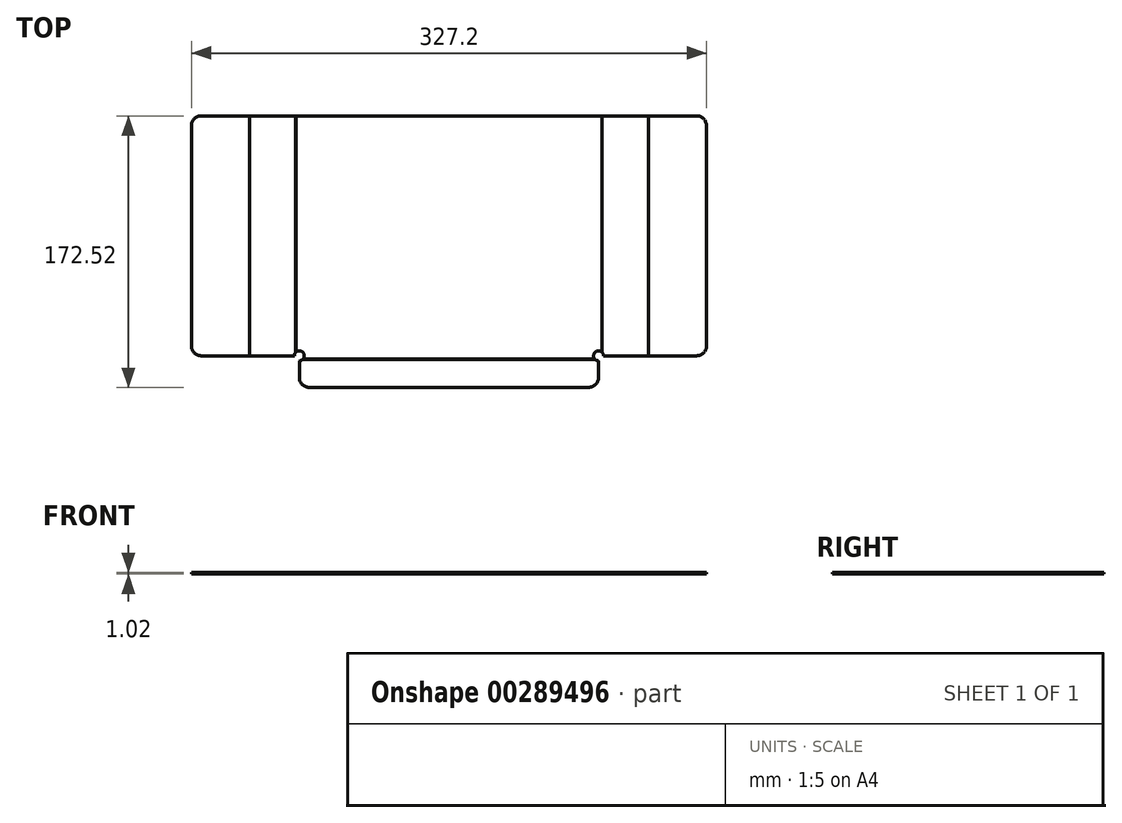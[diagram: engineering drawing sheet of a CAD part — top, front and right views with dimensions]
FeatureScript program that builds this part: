
annotation { "Feature Type Name" : "Feature", "Feature Type Description" : "" }
export const myFeature = defineFeature(function(context is Context, id is Id, definition is map)
    precondition{}
    {
        {
            var Q0;
            Q0=qCreatedBy(makeId("Top.planeOp"),FACE);
            var sketch = newSketch(context, id + "F0", { "sketchPlane" : qUnion([Q0])});
            skLineSegment(sketch, "E0", {"start": v(-95.02, 0) * mm, "end": v(95.02, 0) * mm});
            skPoint(sketch, "E1", {"position": v(0, 0) * mm});
            skLineSegment(sketch, "E2", {"start": v(95.02, 0) * mm, "end": v(99.5, 0) * mm});
            skLineSegment(sketch, "E3", {"start": v(99.5, 0) * mm, "end": v(124.43, 0) * mm});
            skLineSegment(sketch, "E4", {"start": v(124.43, 0) * mm, "end": v(128.9, 0) * mm});
            skLineSegment(sketch, "E5", {"start": v(128.9, 0) * mm, "end": v(157.25, 0) * mm});
            skLineSegment(sketch, "E6", {"start": v(163.6, 6.35) * mm, "end": v(163.6, 146.05) * mm});
            skLineSegment(sketch, "E7", {"start": v(157.25, 152.4) * mm, "end": v(128.9, 152.4) * mm});
            skLineSegment(sketch, "E8", {"start": v(128.9, 152.4) * mm, "end": v(124.43, 152.4) * mm});
            skLineSegment(sketch, "E9", {"start": v(124.43, 152.4) * mm, "end": v(99.5, 152.4) * mm});
            skLineSegment(sketch, "E10", {"start": v(99.5, 152.4) * mm, "end": v(95.02, 152.4) * mm});
            skLineSegment(sketch, "E11", {"start": v(95.02, 152.4) * mm, "end": v(-95.02, 152.4) * mm});
            skLineSegment(sketch, "E12", {"start": v(0, 0) * mm, "end": v(0, 152.4) * mm, "construction": true});
            skLineSegment(sketch, "E13.MirrorCS", {"start": v(-99.5, 152.4) * mm, "end": v(-95.02, 152.4) * mm});
            skLineSegment(sketch, "E14.MirrorCS", {"start": v(-124.43, 152.4) * mm, "end": v(-99.5, 152.4) * mm});
            skLineSegment(sketch, "E15.MirrorCS", {"start": v(-128.9, 152.4) * mm, "end": v(-124.43, 152.4) * mm});
            skLineSegment(sketch, "E16.MirrorCS", {"start": v(-157.25, 152.4) * mm, "end": v(-128.9, 152.4) * mm});
            skLineSegment(sketch, "E17.MirrorCS", {"start": v(-163.6, 6.35) * mm, "end": v(-163.6, 146.05) * mm});
            skLineSegment(sketch, "E18.MirrorCS", {"start": v(-128.9, 0) * mm, "end": v(-157.25, 0) * mm});
            skLineSegment(sketch, "E19.MirrorCS", {"start": v(-124.43, 0) * mm, "end": v(-128.9, 0) * mm});
            skLineSegment(sketch, "E20.MirrorCS", {"start": v(-99.5, 0) * mm, "end": v(-124.43, 0) * mm});
            skLineSegment(sketch, "E21.MirrorCS", {"start": v(-95.02, 0) * mm, "end": v(-99.5, 0) * mm});
            skPoint(sketch, "E22", {"position": v(126.67, 0) * mm});
            skPoint(sketch, "E23", {"position": v(97.26, 0) * mm});
            skPoint(sketch, "E24", {"position": v(-97.26, 0) * mm});
            skPoint(sketch, "E25", {"position": v(-126.67, 0) * mm});
            skLineSegment(sketch, "E26", {"start": v(-126.67, 0) * mm, "end": v(-126.67, 152.4) * mm, "construction": true});
            skLineSegment(sketch, "E27", {"start": v(-97.26, 0) * mm, "end": v(-97.26, 152.4) * mm, "construction": true});
            skLineSegment(sketch, "E28", {"start": v(97.26, 0) * mm, "end": v(97.26, 152.4) * mm, "construction": true});
            skLineSegment(sketch, "E29", {"start": v(126.67, 0) * mm, "end": v(126.67, 152.4) * mm, "construction": true});
            skLineSegment(sketch, "E30.bottom", {"start": v(-97.32, 152.4) * mm, "end": v(-97.2, 152.4) * mm});
            skLineSegment(sketch, "E30.top", {"start": v(-97.32, 0) * mm, "end": v(-97.2, 0) * mm});
            skLineSegment(sketch, "E30.left", {"start": v(-97.32, 152.4) * mm, "end": v(-97.32, 0) * mm});
            skLineSegment(sketch, "E30.right", {"start": v(-97.2, 152.4) * mm, "end": v(-97.2, 0) * mm});
            skPoint(sketch, "E31", {"position": v(-97.26, 152.4) * mm});
            skLineSegment(sketch, "E32.bottom", {"start": v(-126.73, 152.4) * mm, "end": v(-126.6, 152.4) * mm});
            skLineSegment(sketch, "E32.top", {"start": v(-126.73, 0) * mm, "end": v(-126.6, 0) * mm});
            skLineSegment(sketch, "E32.left", {"start": v(-126.73, 152.4) * mm, "end": v(-126.73, 0) * mm});
            skLineSegment(sketch, "E32.right", {"start": v(-126.6, 152.4) * mm, "end": v(-126.6, 0) * mm});
            skLineSegment(sketch, "E33.MirrorCS", {"start": v(97.2, 152.4) * mm, "end": v(97.2, 0) * mm});
            skLineSegment(sketch, "E34.MirrorCS", {"start": v(97.32, 152.4) * mm, "end": v(97.32, 0) * mm});
            skLineSegment(sketch, "E35.MirrorCS", {"start": v(126.6, 152.4) * mm, "end": v(126.6, 0) * mm});
            skLineSegment(sketch, "E36.MirrorCS", {"start": v(126.73, 152.4) * mm, "end": v(126.73, 0) * mm});
            skPoint(sketch, "E37.visualSharp", {"position": v(163.6, 152.4) * mm});
            skArc(sketch, "E37.filletArc", {"start": v(163.6, 146.05) * mm, "mid": v(161.74, 150.54) * mm, "end": v(157.25, 152.4) * mm});
            skPoint(sketch, "E38.visualSharp", {"position": v(163.6, 0) * mm});
            skArc(sketch, "E38.filletArc", {"start": v(157.25, 0) * mm, "mid": v(161.74, 1.86) * mm, "end": v(163.6, 6.35) * mm});
            skPoint(sketch, "E39.visualSharp", {"position": v(-163.6, 0) * mm});
            skArc(sketch, "E39.filletArc", {"start": v(-163.6, 6.35) * mm, "mid": v(-161.74, 1.86) * mm, "end": v(-157.25, 0) * mm});
            skPoint(sketch, "E40.visualSharp", {"position": v(-163.6, 152.4) * mm});
            skArc(sketch, "E40.filletArc", {"start": v(-157.25, 152.4) * mm, "mid": v(-161.74, 150.54) * mm, "end": v(-163.6, 146.05) * mm});
            skLineSegment(sketch, "E41.top", {"start": v(-95.02, -4.47) * mm, "end": v(95.02, -4.47) * mm});
            skLineSegment(sketch, "E41.left", {"start": v(-95.02, 0) * mm, "end": v(-95.02, -4.47) * mm});
            skLineSegment(sketch, "E41.right", {"start": v(95.02, 0) * mm, "end": v(95.02, -4.47) * mm});
            skLineSegment(sketch, "E42.bottom", {"start": v(95.02, -4.47) * mm, "end": v(-95.02, -4.47) * mm});
            skLineSegment(sketch, "E42.top", {"start": v(88.67, -20.12) * mm, "end": v(-88.67, -20.12) * mm});
            skLineSegment(sketch, "E42.left", {"start": v(95.02, -4.47) * mm, "end": v(95.02, -13.77) * mm});
            skLineSegment(sketch, "E42.right", {"start": v(-95.02, -4.47) * mm, "end": v(-95.02, -13.77) * mm});
            skPoint(sketch, "E43", {"position": v(-95.02, -2.24) * mm});
            skLineSegment(sketch, "E44.bottom", {"start": v(-95.02, -2.17) * mm, "end": v(95.02, -2.17) * mm});
            skLineSegment(sketch, "E44.top", {"start": v(-95.02, -2.3) * mm, "end": v(95.02, -2.3) * mm});
            skLineSegment(sketch, "E44.left", {"start": v(-95.02, -2.17) * mm, "end": v(-95.02, -2.3) * mm});
            skLineSegment(sketch, "E44.right", {"start": v(95.02, -2.17) * mm, "end": v(95.02, -2.3) * mm});
            skLineSegment(sketch, "E45", {"start": v(-95.02, -2.24) * mm, "end": v(95.02, -2.24) * mm, "construction": true});
            skPoint(sketch, "E46.visualSharp", {"position": v(-95.02, -20.12) * mm});
            skArc(sketch, "E46.filletArc", {"start": v(-95.02, -13.77) * mm, "mid": v(-93.16, -18.26) * mm, "end": v(-88.67, -20.12) * mm});
            skPoint(sketch, "E47.visualSharp", {"position": v(95.02, -20.12) * mm});
            skArc(sketch, "E47.filletArc", {"start": v(88.67, -20.12) * mm, "mid": v(93.16, -18.26) * mm, "end": v(95.02, -13.77) * mm});
            skSolve(sketch);
        }
        {
            var Q0;
            Q0=qSketchRegion(id+"F0",true);
            extrude(context, id + "F1", {"entities" : qUnion([Q0]), "depth" : 1.02 * mm});
        }
        {
            var Q0;
            Q0=makeQuery(id+"F1.opExtrude","CAP_FACE",FACE,{"disambiguationData":[OSD([sQuery(id+"F0.wireOp",EDGE,"E2"),sQuery(id+"F0.wireOp",EDGE,"E3"),sQuery(id+"F0.wireOp",EDGE,"E4"),sQuery(id+"F0.wireOp",EDGE,"E5"),sQuery(id+"F0.wireOp",EDGE,"E6"),sQuery(id+"F0.wireOp",EDGE,"E7"),sQuery(id+"F0.wireOp",EDGE,"E8"),sQuery(id+"F0.wireOp",EDGE,"E9"),sQuery(id+"F0.wireOp",EDGE,"E10"),sQuery(id+"F0.wireOp",EDGE,"E11"),sQuery(id+"F0.wireOp",EDGE,"E13.MirrorCS"),sQuery(id+"F0.wireOp",EDGE,"E14.MirrorCS"),sQuery(id+"F0.wireOp",EDGE,"E15.MirrorCS"),sQuery(id+"F0.wireOp",EDGE,"E16.MirrorCS"),sQuery(id+"F0.wireOp",EDGE,"E17.MirrorCS"),sQuery(id+"F0.wireOp",EDGE,"E18.MirrorCS"),sQuery(id+"F0.wireOp",EDGE,"E19.MirrorCS"),sQuery(id+"F0.wireOp",EDGE,"E20.MirrorCS"),sQuery(id+"F0.wireOp",EDGE,"E21.MirrorCS"),sQuery(id+"F0.wireOp",EDGE,"E30.bottom"),sQuery(id+"F0.wireOp",EDGE,"E30.top"),sQuery(id+"F0.wireOp",EDGE,"E32.bottom"),sQuery(id+"F0.wireOp",EDGE,"E32.top"),sQuery(id+"F0.wireOp",EDGE,"E37.filletArc"),sQuery(id+"F0.wireOp",EDGE,"E38.filletArc"),sQuery(id+"F0.wireOp",EDGE,"E39.filletArc"),sQuery(id+"F0.wireOp",EDGE,"E40.filletArc"),sQuery(id+"F0.wireOp",EDGE,"E41.left"),sQuery(id+"F0.wireOp",EDGE,"E41.right"),sQuery(id+"F0.wireOp",EDGE,"E42.top"),sQuery(id+"F0.wireOp",EDGE,"E42.left"),sQuery(id+"F0.wireOp",EDGE,"E42.right"),sQuery(id+"F0.wireOp",EDGE,"E44.left"),sQuery(id+"F0.wireOp",EDGE,"E44.right"),sQuery(id+"F0.wireOp",EDGE,"E46.filletArc"),sQuery(id+"F0.wireOp",EDGE,"E47.filletArc")])],"isStart":false});
            var sketch = newSketch(context, id + "F2", { "sketchPlane" : qUnion([Q0])});
            skLineSegment(sketch, "E48.0", {"start": v(-126.6, 152.4) * mm, "end": v(-126.6, 0) * mm});
            skLineSegment(sketch, "E49.0", {"start": v(-126.73, 152.4) * mm, "end": v(-126.73, 0) * mm});
            skLineSegment(sketch, "E50.0", {"start": v(-126.73, 152.4) * mm, "end": v(-126.6, 152.4) * mm});
            skLineSegment(sketch, "E51.0", {"start": v(-124.43, 0) * mm, "end": v(-128.9, 0) * mm});
            skLineSegment(sketch, "E52.0", {"start": v(-97.2, 152.4) * mm, "end": v(-97.2, 0) * mm});
            skLineSegment(sketch, "E53.0", {"start": v(-97.32, 152.4) * mm, "end": v(-97.32, 0) * mm});
            skLineSegment(sketch, "E54.0", {"start": v(97.32, 152.4) * mm, "end": v(97.32, 0) * mm});
            skLineSegment(sketch, "E55.0", {"start": v(97.2, 152.4) * mm, "end": v(97.2, 0) * mm});
            skLineSegment(sketch, "E56.0", {"start": v(126.6, 152.4) * mm, "end": v(126.6, 0) * mm});
            skLineSegment(sketch, "E57.0", {"start": v(126.73, 152.4) * mm, "end": v(126.73, 0) * mm});
            skLineSegment(sketch, "E58.0", {"start": v(-95.02, -2.3) * mm, "end": v(95.02, -2.3) * mm});
            skLineSegment(sketch, "E59.0", {"start": v(-95.02, -2.17) * mm, "end": v(95.02, -2.17) * mm});
            skLineSegment(sketch, "E60", {"start": v(95.02, -2.3) * mm, "end": v(95.02, -2.17) * mm});
            skLineSegment(sketch, "E61", {"start": v(97.2, 0) * mm, "end": v(97.32, 0) * mm});
            skLineSegment(sketch, "E62", {"start": v(126.6, 0) * mm, "end": v(126.73, 0) * mm});
            skLineSegment(sketch, "E63", {"start": v(-95.02, -2.3) * mm, "end": v(-95.02, -2.17) * mm});
            skLineSegment(sketch, "E64", {"start": v(-97.2, 0) * mm, "end": v(-97.32, 0) * mm});
            skLineSegment(sketch, "E65", {"start": v(126.6, 152.4) * mm, "end": v(126.73, 152.4) * mm});
            skLineSegment(sketch, "E66", {"start": v(97.2, 152.4) * mm, "end": v(97.32, 152.4) * mm});
            skLineSegment(sketch, "E67", {"start": v(-97.32, 152.4) * mm, "end": v(-97.2, 152.4) * mm});
            skSolve(sketch);
        }
        {
            var Q0;
            Q0=qSketchRegion(id+"F2",true);
            extrude(context, id + "F3", {"entities" : qUnion([Q0]), "operationType" : NewBodyOperationType.REMOVE, "oppositeDirection" : true, "depth" : 0.5 * mm});
        }
        {
            var Q0;
            {var subQ0=sQuery(id+"F0.wireOp",EDGE,"E44.left");var subQ1=sQuery(id+"F0.wireOp",EDGE,"E42.right");var subQ2=sQuery(id+"F0.wireOp",EDGE,"E41.left");var subQ3=sQuery(id+"F0.wireOp",EDGE,"E5");var subQ4=sQuery(id+"F0.wireOp",EDGE,"E4");var subQ5=sQuery(id+"F0.wireOp",EDGE,"E3");var subQ6=sQuery(id+"F0.wireOp",EDGE,"E2");var subQ7=sQuery(id+"F0.wireOp",EDGE,"E32.top");var subQ8=sQuery(id+"F0.wireOp",EDGE,"E30.top");var subQ9=sQuery(id+"F0.wireOp",EDGE,"E21.MirrorCS");var subQ10=sQuery(id+"F0.wireOp",EDGE,"E20.MirrorCS");var subQ11=sQuery(id+"F0.wireOp",EDGE,"E19.MirrorCS");var subQ12=sQuery(id+"F0.wireOp",EDGE,"E18.MirrorCS");var subQ13=sQuery(id+"F0.wireOp",EDGE,"E32.bottom");var subQ14=sQuery(id+"F0.wireOp",EDGE,"E30.bottom");var subQ15=sQuery(id+"F0.wireOp",EDGE,"E16.MirrorCS");var subQ16=sQuery(id+"F0.wireOp",EDGE,"E15.MirrorCS");var subQ17=sQuery(id+"F0.wireOp",EDGE,"E14.MirrorCS");var subQ18=sQuery(id+"F0.wireOp",EDGE,"E13.MirrorCS");var subQ19=sQuery(id+"F0.wireOp",EDGE,"E11");var subQ20=sQuery(id+"F0.wireOp",EDGE,"E10");var subQ21=sQuery(id+"F0.wireOp",EDGE,"E9");var subQ22=sQuery(id+"F0.wireOp",EDGE,"E8");var subQ23=sQuery(id+"F0.wireOp",EDGE,"E7");var subQ24=sQuery(id+"F0.wireOp",EDGE,"E44.right");var subQ25=sQuery(id+"F0.wireOp",EDGE,"E42.left");var subQ26=sQuery(id+"F0.wireOp",EDGE,"E41.right");Q0=makeQuery(id+"F3.boolean.opBoolean","SPLIT",FACE,{"disambiguationData":[TD([makeQuery(id+"F3.opExtrude","SWEPT_FACE",FACE,{"disambiguationData":[OSD([sQuery(id+"F2.wireOp",EDGE,"E52.0")])]})])],"derivedFrom":makeQuery(id+"F1.opExtrude","CAP_FACE",FACE,{"disambiguationData":[OSD([subQ6,subQ5,subQ4,subQ3,sQuery(id+"F0.wireOp",EDGE,"E6"),subQ23,subQ22,subQ21,subQ20,subQ19,subQ18,subQ17,subQ16,subQ15,sQuery(id+"F0.wireOp",EDGE,"E17.MirrorCS"),subQ12,subQ11,subQ10,subQ9,subQ14,subQ8,subQ13,subQ7,sQuery(id+"F0.wireOp",EDGE,"E37.filletArc"),sQuery(id+"F0.wireOp",EDGE,"E38.filletArc"),sQuery(id+"F0.wireOp",EDGE,"E39.filletArc"),sQuery(id+"F0.wireOp",EDGE,"E40.filletArc"),subQ2,subQ26,sQuery(id+"F0.wireOp",EDGE,"E42.top"),subQ25,subQ1,subQ0,subQ24,sQuery(id+"F0.wireOp",EDGE,"E46.filletArc"),sQuery(id+"F0.wireOp",EDGE,"E47.filletArc")])],"isStart":false})});}
            var sketch = newSketch(context, id + "F4", { "sketchPlane" : qUnion([Q0])});
            skPoint(sketch, "E68.0", {"position": v(-95.02, 0) * mm});
            skPoint(sketch, "E69.0", {"position": v(95.02, 0) * mm});
            skSolve(sketch);
        }
        {
            var Q0;
            Q0=sQuery(id+"F4.wireOp",VERTEX,"E69.0");
            var Q1;
            Q1=sQuery(id+"F4.wireOp",VERTEX,"E68.0");
            var Q2;
            Q2=makeQuery(id+"F1.opExtrude","SWEPT_BODY",BODY,{"disambiguationData":[OSD([sQuery(id+"F0.wireOp",EDGE,"E2"),sQuery(id+"F0.wireOp",EDGE,"E3"),sQuery(id+"F0.wireOp",EDGE,"E4"),sQuery(id+"F0.wireOp",EDGE,"E5"),sQuery(id+"F0.wireOp",EDGE,"E6"),sQuery(id+"F0.wireOp",EDGE,"E7"),sQuery(id+"F0.wireOp",EDGE,"E8"),sQuery(id+"F0.wireOp",EDGE,"E9"),sQuery(id+"F0.wireOp",EDGE,"E10"),sQuery(id+"F0.wireOp",EDGE,"E11"),sQuery(id+"F0.wireOp",EDGE,"E13.MirrorCS"),sQuery(id+"F0.wireOp",EDGE,"E14.MirrorCS"),sQuery(id+"F0.wireOp",EDGE,"E15.MirrorCS"),sQuery(id+"F0.wireOp",EDGE,"E16.MirrorCS"),sQuery(id+"F0.wireOp",EDGE,"E17.MirrorCS"),sQuery(id+"F0.wireOp",EDGE,"E18.MirrorCS"),sQuery(id+"F0.wireOp",EDGE,"E19.MirrorCS"),sQuery(id+"F0.wireOp",EDGE,"E20.MirrorCS"),sQuery(id+"F0.wireOp",EDGE,"E21.MirrorCS"),sQuery(id+"F0.wireOp",EDGE,"E30.bottom"),sQuery(id+"F0.wireOp",EDGE,"E30.top"),sQuery(id+"F0.wireOp",EDGE,"E32.bottom"),sQuery(id+"F0.wireOp",EDGE,"E32.top"),sQuery(id+"F0.wireOp",EDGE,"E37.filletArc"),sQuery(id+"F0.wireOp",EDGE,"E38.filletArc"),sQuery(id+"F0.wireOp",EDGE,"E39.filletArc"),sQuery(id+"F0.wireOp",EDGE,"E40.filletArc"),sQuery(id+"F0.wireOp",EDGE,"E41.left"),sQuery(id+"F0.wireOp",EDGE,"E41.right"),sQuery(id+"F0.wireOp",EDGE,"E42.top"),sQuery(id+"F0.wireOp",EDGE,"E42.left"),sQuery(id+"F0.wireOp",EDGE,"E42.right"),sQuery(id+"F0.wireOp",EDGE,"E44.left"),sQuery(id+"F0.wireOp",EDGE,"E44.right"),sQuery(id+"F0.wireOp",EDGE,"E46.filletArc"),sQuery(id+"F0.wireOp",EDGE,"E47.filletArc")])]});
            hole(context, id + "F5", {"style" : HoleStyle.SIMPLE, "endStyle" : HoleEndStyle.THROUGH, "holeDiameter" : 6.35 * mm, "isTappedThrough" : true, "tappedDepth" : 12.7 * mm, "tapClearance" : 3, "locations" : qUnion([Q0, Q1]), "scope" : qUnion([Q2]), "startStyle" : HoleStartStyle.PART});
        }
    });
